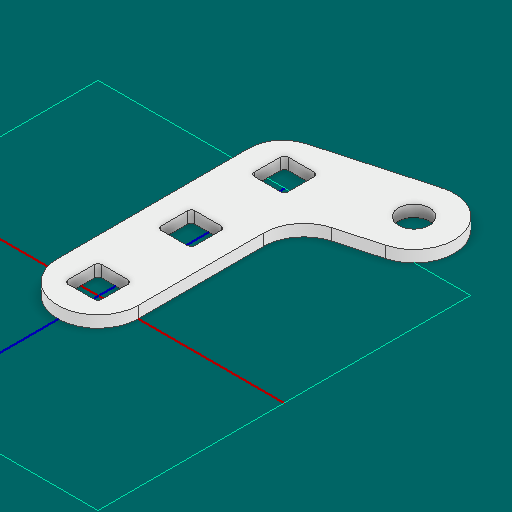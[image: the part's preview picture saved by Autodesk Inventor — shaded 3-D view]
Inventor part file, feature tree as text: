
AUTODESK INVENTOR PART (.ipt)
format: ipt  version: 2025 (Build 290162000, 162)  size: 143,360 bytes
history: native  units: in
note: dims shown in document units (in); Inventor stores cm internally (conversion verified against a paired STEP export)
features: other x3, extrude x1, sketch x1
ambient origin geometry x8: Origin, YZ Plane, XZ Plane, XY Plane, X Axis, Y Axis, Z Axis, Center Point
bodies: Solid1 (feature_tree)
feature tree (5):
  other  "Blocks"
  extrude  "Extrusion1"  Depth=0.5in
  sketch  "Sketch1"  dims[d0=0.0625in d1=0.0in d3=0.5in d4=0.0344in d5=0.5in d6=0.0344in]
  other  "main"
  other  "main:1"
